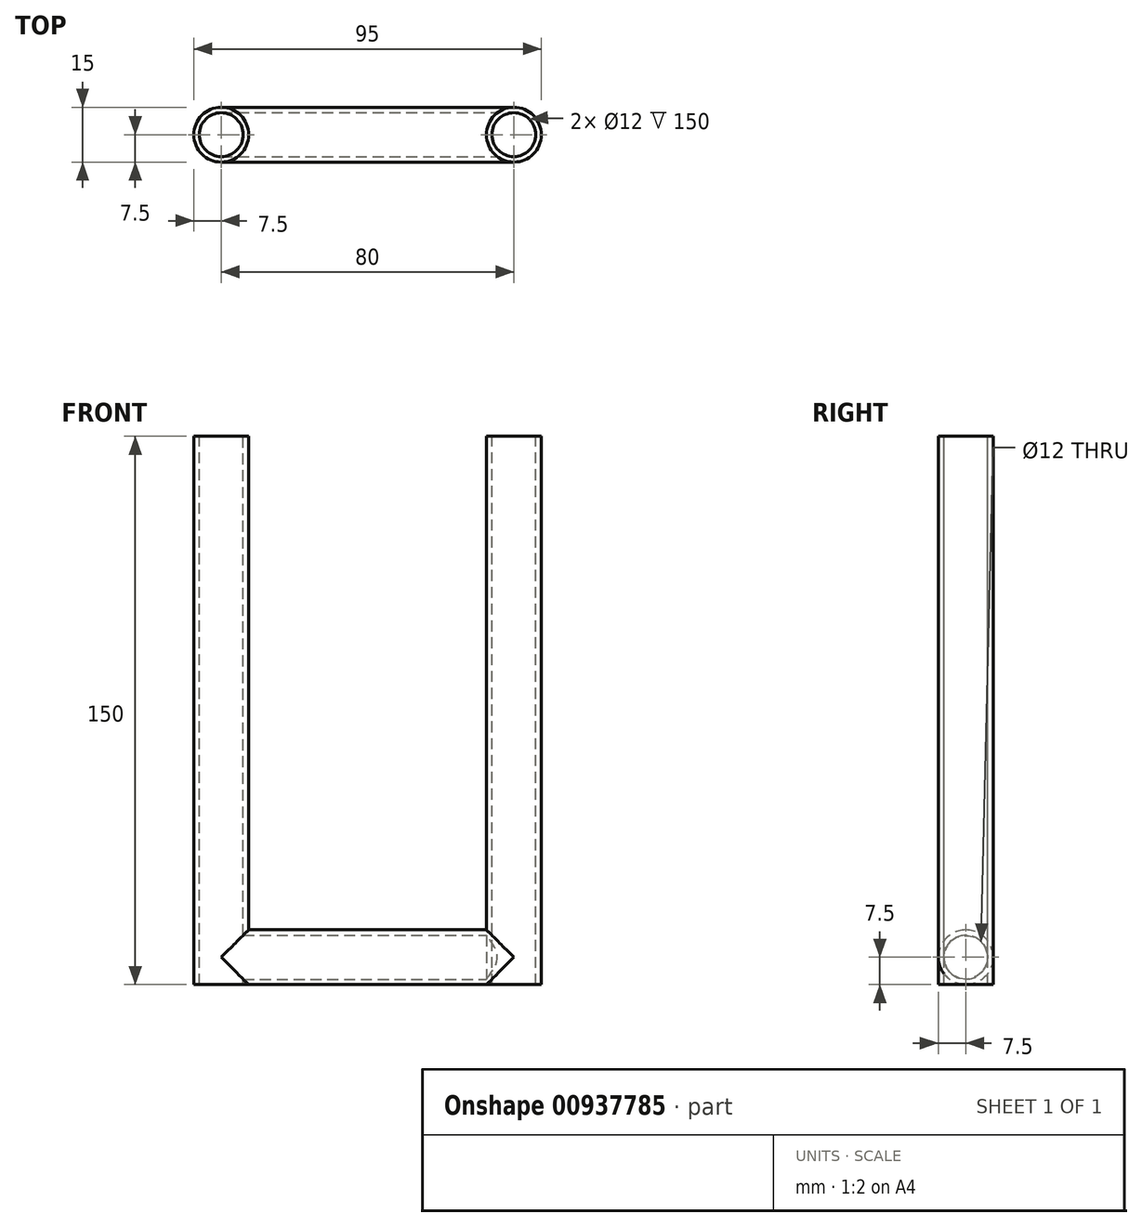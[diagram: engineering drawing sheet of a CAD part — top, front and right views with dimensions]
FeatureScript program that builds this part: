
annotation { "Feature Type Name" : "Feature", "Feature Type Description" : "" }
export const myFeature = defineFeature(function(context is Context, id is Id, definition is map)
    precondition{}
    {
        {
            var Q0;
            Q0=qCreatedBy(makeId("Top.planeOp"),FACE);
            var sketch = newSketch(context, id + "F0", { "sketchPlane" : qUnion([Q0])});
            skCircle(sketch, "E0", {"center": v(0, 0) * mm, "radius": 7.5 * mm});
            skSolve(sketch);
        }
        {
            var Q0;
            Q0=qSketchRegion(id+"F0",true);
            extrude(context, id + "F1", {"entities" : qUnion([Q0]), "depth" : 150 * mm, "offsetDistance" : 25 * mm});
        }
        {
            var Q0;
            Q0=makeQuery(id+"F1.opExtrude","CAP_FACE",FACE,{"disambiguationData":[OSD([sQuery(id+"F0.wireOp",EDGE,"E0")])],"isStart":false});
            var sketch = newSketch(context, id + "F2", { "sketchPlane" : qUnion([Q0])});
            skCircle(sketch, "E1", {"center": v(0, 0) * mm, "radius": 6 * mm});
            skSolve(sketch);
        }
        {
            var Q0;
            Q0=qSketchRegion(id+"F2",true);
            extrude(context, id + "F3", {"entities" : qUnion([Q0]), "operationType" : NewBodyOperationType.REMOVE, "oppositeDirection" : true, "depth" : 300 * mm, "offsetDistance" : 25 * mm});
        }
        {
            var Q0;
            Q0=qCreatedBy(makeId("Right.planeOp"),FACE);
            var sketch = newSketch(context, id + "F4", { "sketchPlane" : qUnion([Q0])});
            skCircle(sketch, "E2", {"center": v(0, 7.5) * mm, "radius": 7.5 * mm});
            skSolve(sketch);
        }
        {
            var Q0;
            Q0=qSketchRegion(id+"F4",true);
            extrude(context, id + "F5", {"entities" : qUnion([Q0]), "operationType" : NewBodyOperationType.ADD, "depth" : 80 * mm, "offsetDistance" : 25 * mm});
        }
        {
            var Q0;
            Q0=makeQuery(id+"F5.opExtrude","CAP_FACE",FACE,{"disambiguationData":[OSD([sQuery(id+"F4.wireOp",EDGE,"E2")])],"isStart":false});
            var sketch = newSketch(context, id + "F6", { "sketchPlane" : qUnion([Q0])});
            skCircle(sketch, "E3", {"center": v(0, 7.5) * mm, "radius": 6 * mm});
            skSolve(sketch);
        }
        {
            var Q0;
            Q0=qSketchRegion(id+"F6",true);
            extrude(context, id + "F7", {"entities" : qUnion([Q0]), "operationType" : NewBodyOperationType.REMOVE, "oppositeDirection" : true, "depth" : 80 * mm, "offsetDistance" : 25 * mm});
        }
        {
            var Q0;
            Q0=qCreatedBy(makeId("Top.planeOp"),FACE);
            var sketch = newSketch(context, id + "F8", { "sketchPlane" : qUnion([Q0])});
            skCircle(sketch, "E4", {"center": v(80, 0) * mm, "radius": 7.5 * mm});
            skSolve(sketch);
        }
        {
            var Q0;
            Q0=qSketchRegion(id+"F8",true);
            extrude(context, id + "F9", {"entities" : qUnion([Q0]), "operationType" : NewBodyOperationType.ADD, "depth" : 150 * mm, "offsetDistance" : 25 * mm});
        }
        {
            var Q0;
            Q0=makeQuery(id+"F9.opExtrude","CAP_FACE",FACE,{"disambiguationData":[OSD([sQuery(id+"F8.wireOp",EDGE,"E4")])],"isStart":false});
            var sketch = newSketch(context, id + "F10", { "sketchPlane" : qUnion([Q0])});
            skCircle(sketch, "E5", {"center": v(80, 0) * mm, "radius": 6 * mm});
            skSolve(sketch);
        }
        {
            var Q0;
            Q0=qSketchRegion(id+"F10",true);
            extrude(context, id + "F11", {"entities" : qUnion([Q0]), "operationType" : NewBodyOperationType.REMOVE, "oppositeDirection" : true, "depth" : 300 * mm, "offsetDistance" : 25 * mm});
        }
        {
            var Q0;
            Q0=qCreatedBy(makeId("Top.planeOp"),FACE);
            var sketch = newSketch(context, id + "F12", { "sketchPlane" : qUnion([Q0])});
            skCircle(sketch, "E6", {"center": v(0, 0) * mm, "radius": 6 * mm});
            skSolve(sketch);
        }
        {
            var Q0;
            Q0=qSketchRegion(id+"F12",true);
            extrude(context, id + "F13", {"entities" : qUnion([Q0]), "operationType" : NewBodyOperationType.REMOVE, "depth" : 300 * mm, "offsetDistance" : 25 * mm});
        }
    });
